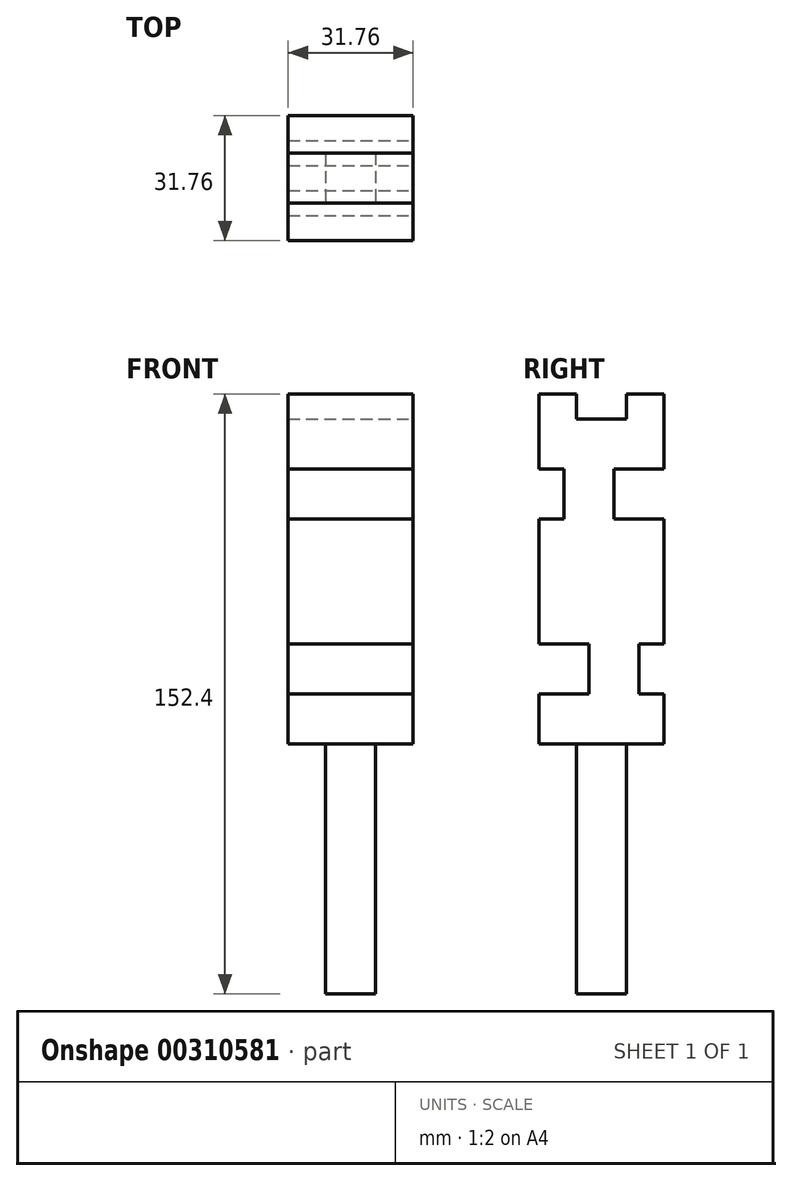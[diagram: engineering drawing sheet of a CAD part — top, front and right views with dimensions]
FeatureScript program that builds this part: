
annotation { "Feature Type Name" : "Feature", "Feature Type Description" : "" }
export const myFeature = defineFeature(function(context is Context, id is Id, definition is map)
    precondition{}
    {
        {
            var Q0;
            Q0=qCreatedBy(makeId("Top.planeOp"),FACE);
            var sketch = newSketch(context, id + "F0", { "sketchPlane" : qUnion([Q0])});
            skLineSegment(sketch, "E0.bottom", {"start": v(15.87, 15.88) * mm, "end": v(-15.88, 15.88) * mm});
            skLineSegment(sketch, "E0.top", {"start": v(15.88, -15.88) * mm, "end": v(-15.87, -15.88) * mm});
            skLineSegment(sketch, "E0.left", {"start": v(15.87, 15.88) * mm, "end": v(15.88, -15.88) * mm});
            skLineSegment(sketch, "E0.right", {"start": v(-15.88, 15.88) * mm, "end": v(-15.87, -15.88) * mm});
            skPoint(sketch, "E0.middle", {"position": v(0, 0) * mm});
            skSolve(sketch);
        }
        {
            var Q0;
            Q0 = qSketchRegion(id + "F0", true);
            extrude(context, id + "F1", {"entities" : qUnion([Q0]), "depth" : 88.9 * mm, "symmetric" : true});
        }
        {
            var Q0;
            Q0=makeQuery(id+"F1.opExtrude","CAP_FACE",FACE,{"disambiguationData":[OSD([sQuery(id+"F0.wireOp",EDGE,"E0.bottom"),sQuery(id+"F0.wireOp",EDGE,"E0.top"),sQuery(id+"F0.wireOp",EDGE,"E0.left"),sQuery(id+"F0.wireOp",EDGE,"E0.right")])],"isStart":true});
            var sketch = newSketch(context, id + "F2", { "sketchPlane" : qUnion([Q0])});
            skLineSegment(sketch, "E1.bottom", {"start": v(-6.35, -6.35) * mm, "end": v(6.35, -6.35) * mm});
            skLineSegment(sketch, "E1.top", {"start": v(-6.35, 6.35) * mm, "end": v(6.35, 6.35) * mm});
            skLineSegment(sketch, "E1.left", {"start": v(-6.35, -6.35) * mm, "end": v(-6.35, 6.35) * mm});
            skLineSegment(sketch, "E1.right", {"start": v(6.35, -6.35) * mm, "end": v(6.35, 6.35) * mm});
            skPoint(sketch, "E1.middle", {"position": v(0, 0) * mm});
            skSolve(sketch);
        }
        {
            var Q0;
            Q0=makeQuery(id+"F2.imprint","IMPRINT",FACE,{"disambiguationData":[TD([[makeQuery(id+"F2.imprint","IMPRINT",EDGE,{"derivedFrom":sQuery(id+"F2.wireOp",EDGE,"E1.bottom")}),1.0]])]});
            extrude(context, id + "F3", {"entities" : qUnion([Q0]), "operationType" : NewBodyOperationType.ADD, "depth" : 63.5 * mm});
        }
        {
            var Q0;
            Q0=makeQuery(id+"F1.opExtrude","CAP_FACE",FACE,{"disambiguationData":[OSD([sQuery(id+"F0.wireOp",EDGE,"E0.bottom"),sQuery(id+"F0.wireOp",EDGE,"E0.top"),sQuery(id+"F0.wireOp",EDGE,"E0.left"),sQuery(id+"F0.wireOp",EDGE,"E0.right")])],"isStart":false});
            var sketch = newSketch(context, id + "F4", { "sketchPlane" : qUnion([Q0])});
            skLineSegment(sketch, "E2.bottom", {"start": v(-15.87, -6.35) * mm, "end": v(15.88, -6.35) * mm});
            skLineSegment(sketch, "E2.top", {"start": v(-15.87, 6.35) * mm, "end": v(15.88, 6.35) * mm});
            skLineSegment(sketch, "E2.left", {"start": v(-15.87, -6.35) * mm, "end": v(-15.87, 6.35) * mm});
            skLineSegment(sketch, "E2.right", {"start": v(15.88, -6.35) * mm, "end": v(15.88, 6.35) * mm});
            skPoint(sketch, "E2.middle", {"position": v(0, 0) * mm});
            skSolve(sketch);
        }
        {
            var Q0;
            Q0=makeQuery(id+"F4.imprint","IMPRINT",FACE,{"disambiguationData":[TD([[makeQuery(id+"F4.imprint","IMPRINT",EDGE,{"derivedFrom":sQuery(id+"F4.wireOp",EDGE,"E2.bottom")}),1.0]])]});
            extrude(context, id + "F5", {"entities" : qUnion([Q0]), "operationType" : NewBodyOperationType.REMOVE, "oppositeDirection" : true, "depth" : 6.35 * mm});
        }
        {
            var Q0;
            Q0=makeQuery(id+"F1.opExtrude","SWEPT_FACE",FACE,{"disambiguationData":[OSD([sQuery(id+"F0.wireOp",EDGE,"E0.left")])]});
            var sketch = newSketch(context, id + "F6", { "sketchPlane" : qUnion([Q0])});
            skLineSegment(sketch, "E3.bottom", {"start": v(15.88, 25.4) * mm, "end": v(3.17, 25.4) * mm});
            skLineSegment(sketch, "E3.top", {"start": v(15.88, 12.7) * mm, "end": v(3.18, 12.7) * mm});
            skLineSegment(sketch, "E3.left", {"start": v(15.88, 25.4) * mm, "end": v(15.88, 12.7) * mm});
            skLineSegment(sketch, "E3.right", {"start": v(3.17, 25.4) * mm, "end": v(3.18, 12.7) * mm});
            skLineSegment(sketch, "E4.bottom", {"start": v(15.88, -31.75) * mm, "end": v(9.52, -31.75) * mm});
            skLineSegment(sketch, "E4.top", {"start": v(15.87, -19.05) * mm, "end": v(9.52, -19.05) * mm});
            skLineSegment(sketch, "E4.left", {"start": v(15.88, -31.75) * mm, "end": v(15.88, -19.05) * mm});
            skLineSegment(sketch, "E4.right", {"start": v(9.52, -31.75) * mm, "end": v(9.52, -19.05) * mm});
            skLineSegment(sketch, "E5.bottom", {"start": v(-15.88, -31.75) * mm, "end": v(-3.18, -31.75) * mm});
            skLineSegment(sketch, "E5.top", {"start": v(-15.88, -19.05) * mm, "end": v(-3.18, -19.05) * mm});
            skLineSegment(sketch, "E5.left", {"start": v(-15.88, -31.75) * mm, "end": v(-15.88, -19.05) * mm});
            skLineSegment(sketch, "E5.right", {"start": v(-3.18, -31.75) * mm, "end": v(-3.18, -19.05) * mm});
            skLineSegment(sketch, "E6.bottom", {"start": v(-15.88, 12.7) * mm, "end": v(-9.53, 12.7) * mm});
            skLineSegment(sketch, "E6.top", {"start": v(-15.88, 25.4) * mm, "end": v(-9.53, 25.4) * mm});
            skLineSegment(sketch, "E6.left", {"start": v(-15.88, 12.7) * mm, "end": v(-15.88, 25.4) * mm});
            skLineSegment(sketch, "E6.right", {"start": v(-9.53, 12.7) * mm, "end": v(-9.53, 25.4) * mm});
            skSolve(sketch);
        }
        {
            var Q0;
            Q0 = qSketchRegion(id + "F6", true);
            var Q1;
            Q1=makeQuery(id+"F1.opExtrude","SWEPT_FACE",FACE,{"disambiguationData":[OSD([sQuery(id+"F0.wireOp",EDGE,"E0.right")])]});
            extrude(context, id + "F7", {"entities" : qUnion([Q0]), "operationType" : NewBodyOperationType.REMOVE, "endBound" : BoundingType.UP_TO_SURFACE, "oppositeDirection" : true, "endBoundEntityFace" : qUnion([Q1]), "depth" : 25.4 * mm});
        }
    });
